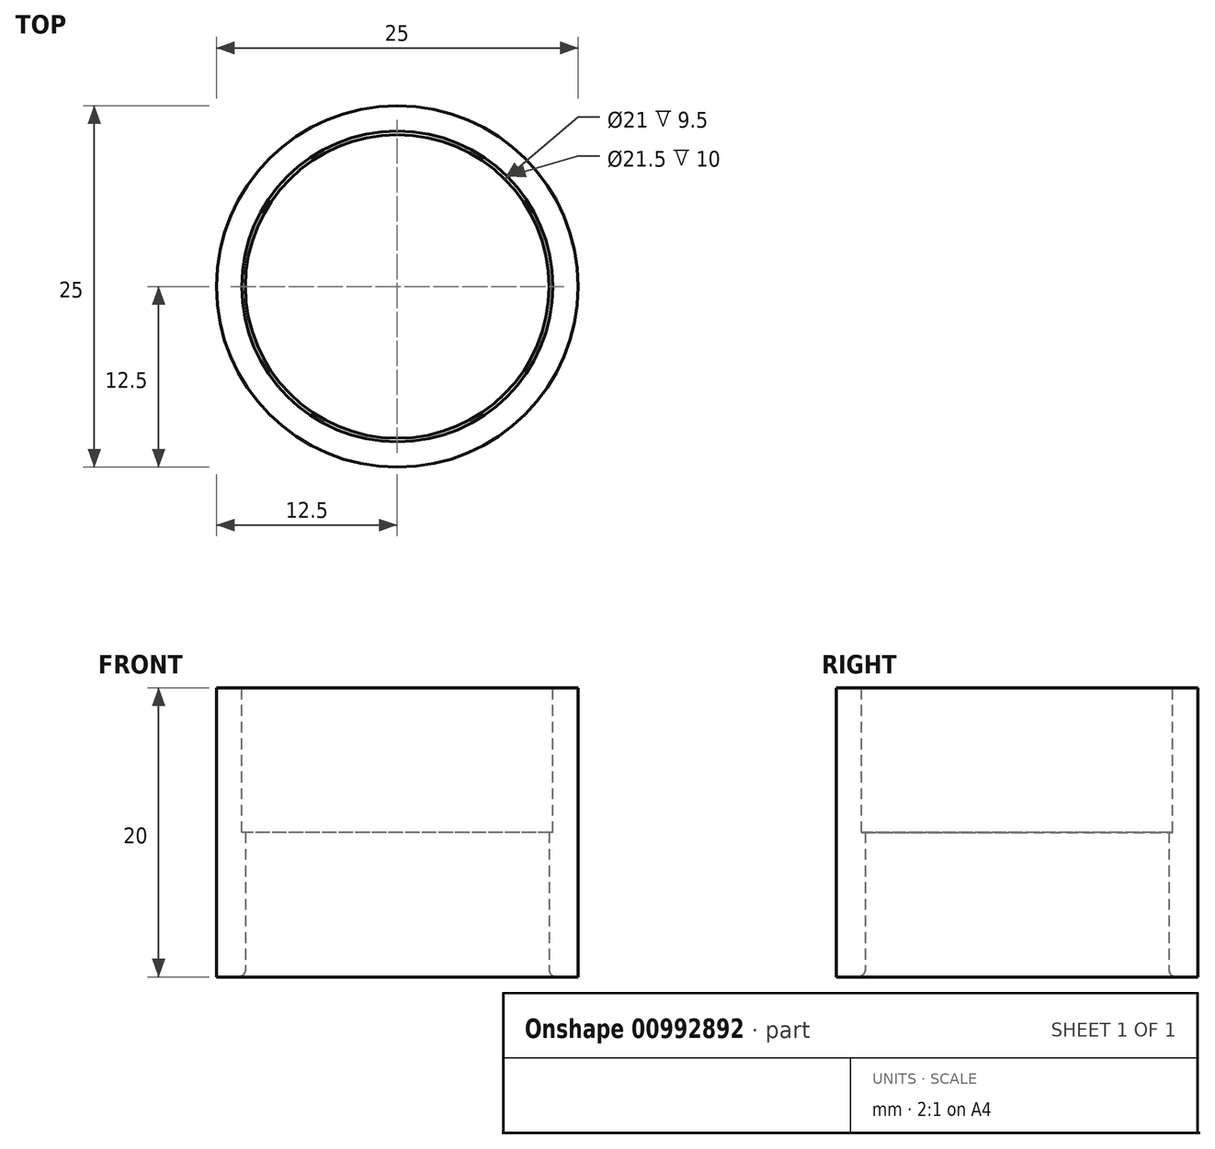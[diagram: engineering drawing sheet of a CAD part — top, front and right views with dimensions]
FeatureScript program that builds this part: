
annotation { "Feature Type Name" : "Feature", "Feature Type Description" : "" }
export const myFeature = defineFeature(function(context is Context, id is Id, definition is map)
    precondition{}
    {
        {
            var Q0;
            Q0=qCreatedBy(makeId("Top.planeOp"),FACE);
            cPlane(context, id + "F0", {"entities" : qUnion([Q0]), "cplaneType" : CPlaneType.OFFSET, "offset" : 36.5 * mm, "width" : 150 * mm, "height" : 150 * mm});
        }
        {
            var Q0;
            Q0=qCreatedBy(id+"F0.planeOp",FACE);
            var sketch = newSketch(context, id + "F1", { "sketchPlane" : qUnion([Q0])});
            skCircle(sketch, "E0", {"center": v(0, 0) * mm, "radius": 10.5 * mm});
            skCircle(sketch, "E1", {"center": v(0, 0) * mm, "radius": 12.5 * mm});
            skSolve(sketch);
        }
        {
            var Q0;
            Q0=qSketchRegion(id+"F1",true);
            extrude(context, id + "F2", {"entities" : qUnion([Q0]), "depth" : 20 * mm});
        }
        {
            var Q0;
            Q0=makeQuery(id+"F2.opExtrude","CAP_FACE",FACE,{"disambiguationData":[OSD([sQuery(id+"F1.wireOp",EDGE,"E0"),sQuery(id+"F1.wireOp",EDGE,"E1")])],"isStart":false});
            var sketch = newSketch(context, id + "F3", { "sketchPlane" : qUnion([Q0])});
            skCircle(sketch, "E2", {"center": v(0, 0) * mm, "radius": 10.75 * mm});
            skSolve(sketch);
        }
        {
            var Q0;
            Q0=qSketchRegion(id+"F3",true);
            extrude(context, id + "F4", {"entities" : qUnion([Q0]), "operationType" : NewBodyOperationType.REMOVE, "oppositeDirection" : true, "depth" : 10 * mm});
        }
        {
            var Q0;
            Q0=makeQuery(id+"F4.boolean.opBoolean","COPY",EDGE,{"derivedFrom":makeQuery(id+"F4.opExtrude","CAP_EDGE",EDGE,{"disambiguationData":[OSD([sQuery(id+"F3.wireOp",EDGE,"E2")])],"isStart":true})});
            var Q1;
            Q1=makeQuery(id+"F2.opExtrude","CAP_EDGE",EDGE,{"disambiguationData":[OSD([sQuery(id+"F1.wireOp",EDGE,"E0")])],"isStart":true});
            fillet(context, id + "F5", {"entities" : qUnion([Q0, Q1]), "radius" : .5 * mm, "tangentPropagation" : true, "allowEdgeOverflow" : false});
        }
    });
